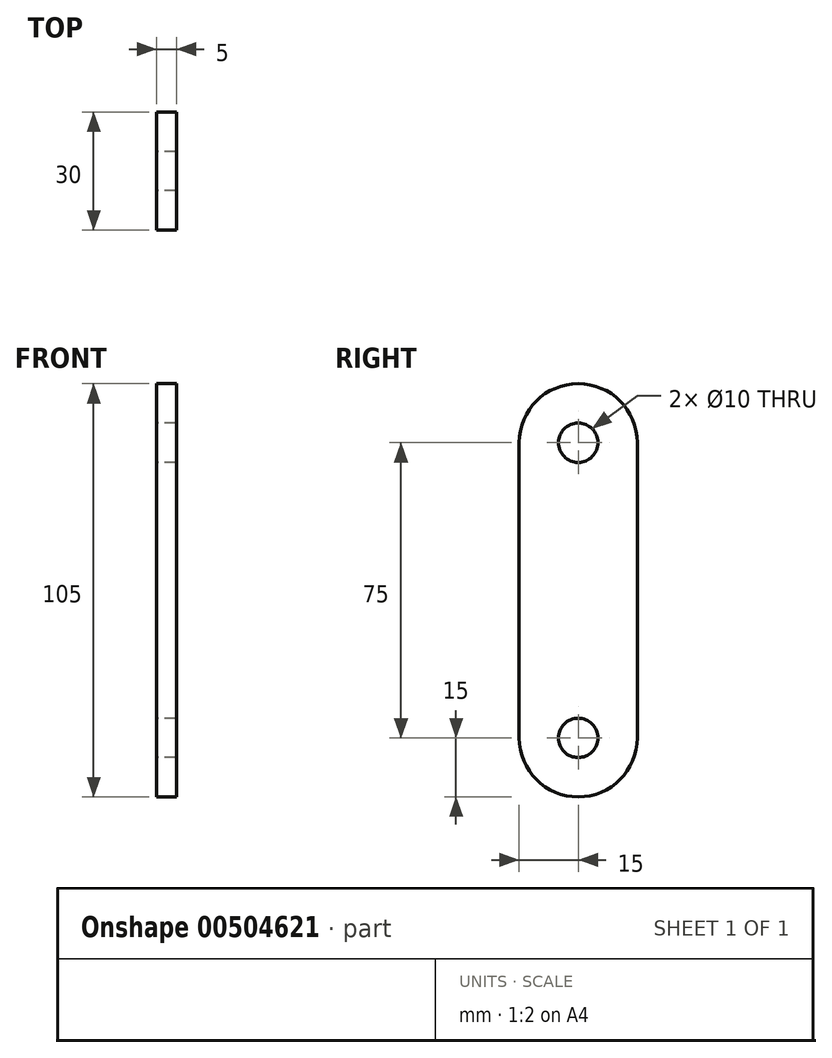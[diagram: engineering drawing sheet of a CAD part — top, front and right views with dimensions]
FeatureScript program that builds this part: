
annotation { "Feature Type Name" : "Feature", "Feature Type Description" : "" }
export const myFeature = defineFeature(function(context is Context, id is Id, definition is map)
    precondition{}
    {
        {
            var Q0;
            Q0=qCreatedBy(makeId("Right.planeOp"),FACE);
            var sketch = newSketch(context, id + "F0", { "sketchPlane" : qUnion([Q0])});
            skCircle(sketch, "E0", {"center": v(0, 0) * mm, "radius": 5 * mm});
            skArc(sketch, "E1", {"start": v(-15, 0) * mm, "mid": v(0, -15) * mm, "end": v(15, 0) * mm});
            skLineSegment(sketch, "E2", {"start": v(0, 0) * mm, "end": v(5, 0) * mm});
            skLineSegment(sketch, "E3", {"start": v(-15, 0) * mm, "end": v(-15, 75) * mm});
            skLineSegment(sketch, "E4", {"start": v(15, 0) * mm, "end": v(15, 75) * mm});
            skCircle(sketch, "E5", {"center": v(0, 75) * mm, "radius": 5 * mm});
            skArc(sketch, "E6", {"start": v(15, 75) * mm, "mid": v(0, 90) * mm, "end": v(-15, 75) * mm});
            skLineSegment(sketch, "E7", {"start": v(0, 0) * mm, "end": v(15, 0) * mm});
            skLineSegment(sketch, "E8", {"start": v(0, 75) * mm, "end": v(15, 75) * mm});
            skLineSegment(sketch, "E9", {"start": v(-15, 75) * mm, "end": v(15, 75) * mm});
            skSolve(sketch);
        }
        {
            var Q0;
            Q0=qSketchRegion(id+"F0",true);
            extrude(context, id + "F1", {"entities" : qUnion([Q0]), "depth" : 5 * mm, "offsetDistance" : 25 * mm});
        }
    });
